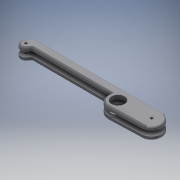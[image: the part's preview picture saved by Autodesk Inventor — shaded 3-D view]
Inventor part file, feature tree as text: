
AUTODESK INVENTOR PART (.ipt)
format: ipt  version: 2017 (Build 210142000, 142)  size: 202,752 bytes
history: native  units: mm
features: extrude x2, sketch x2, fillet x1, plane x1, mirror x1
ambient origin geometry x8: Origin, YZ Plane, XZ Plane, XY Plane, X Axis, Y Axis, Z Axis, Center Point
bodies: Solid1 (feature_tree)
feature tree (7):
  extrude  "Extrusion1"  Depth=4.3mm
  extrude  "Extrusion2"  Depth=6.6mm
  fillet  "Fillet2"  Radius=4.3mm
  plane  "Work Plane1"
  mirror  "Mirror2"
  sketch  "Sketch1"  dims[d0=22.0mm d1=4.3mm]
  sketch  "Sketch2"  dims[d2=160.0mm d3=5.5mm d4=4.3mm d5=54.4mm d6=2.0mm d7=15.0mm d9=6.0mm d12=6.0mm d13=0.0mm d14=1.0mm d15=0.0mm d17=3.0mm d19=-10.3mm d20=6.6mm]
